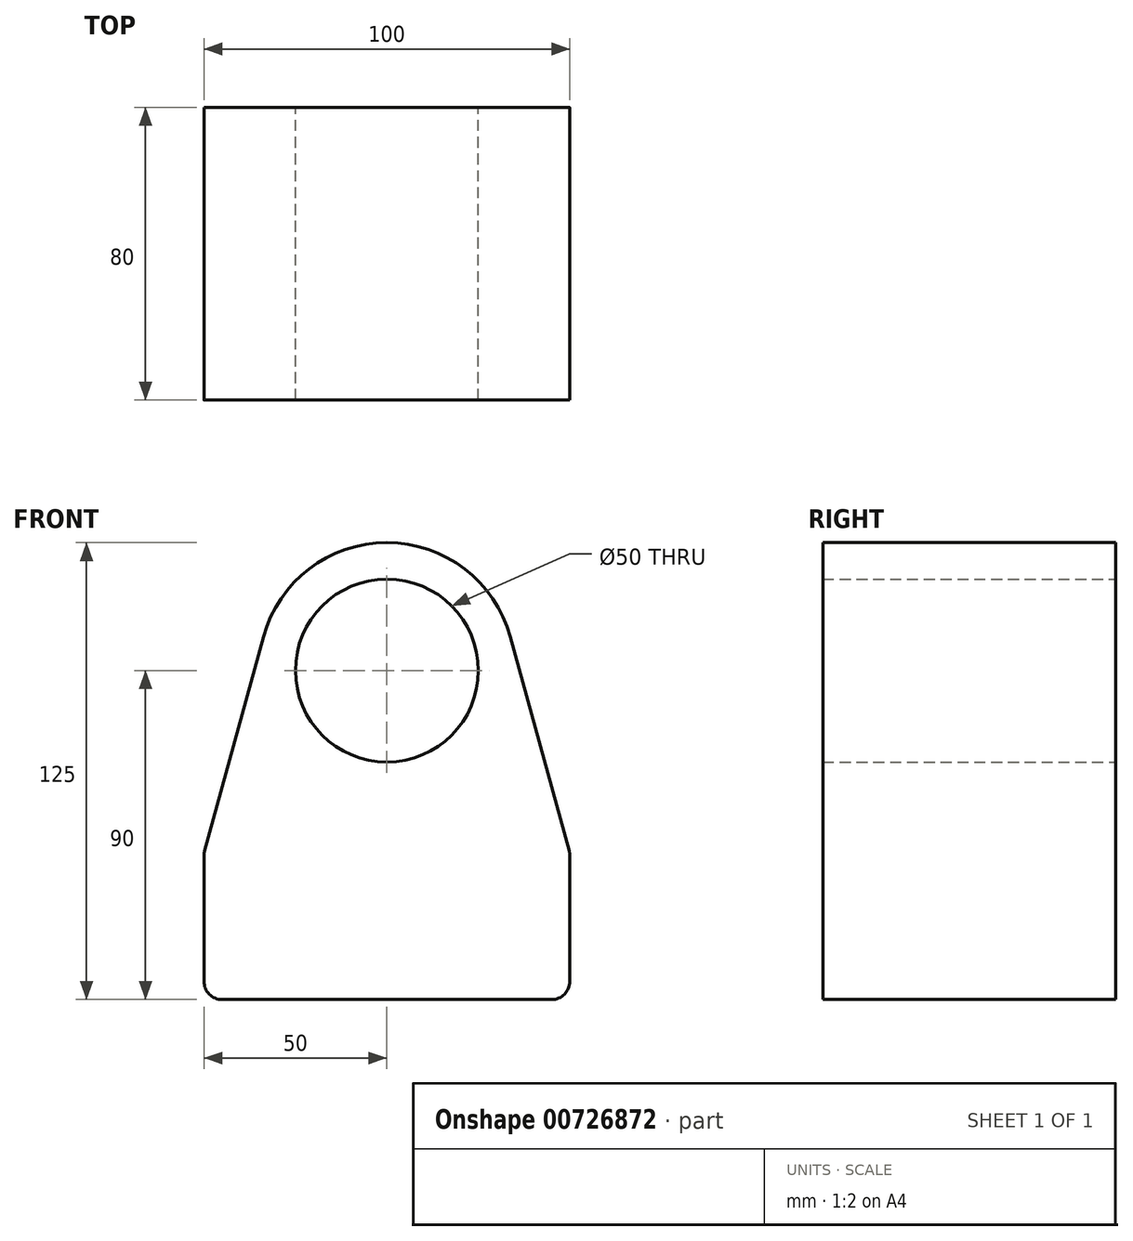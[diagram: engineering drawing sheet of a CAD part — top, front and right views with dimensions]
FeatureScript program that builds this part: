
annotation { "Feature Type Name" : "Feature", "Feature Type Description" : "" }
export const myFeature = defineFeature(function(context is Context, id is Id, definition is map)
    precondition{}
    {
        {
            var Q0;
            Q0=qCreatedBy(makeId("Front.planeOp"),FACE);
            var sketch = newSketch(context, id + "F0", { "sketchPlane" : qUnion([Q0])});
            skLineSegment(sketch, "E0", {"start": v(0, 0) * mm, "end": v(0, 40) * mm});
            skLineSegment(sketch, "E1", {"start": v(100, 40) * mm, "end": v(100, 0) * mm});
            skLineSegment(sketch, "E2", {"start": v(100, 0) * mm, "end": v(0, 0) * mm});
            skCircle(sketch, "E3", {"center": v(50, 90) * mm, "radius": 25 * mm});
            skArc(sketch, "E4", {"start": v(83.75, 99.25) * mm, "mid": v(50, 125) * mm, "end": v(16.25, 99.25) * mm});
            skLineSegment(sketch, "E5", {"start": v(0, 40) * mm, "end": v(16.25, 99.25) * mm});
            skLineSegment(sketch, "E6", {"start": v(100, 40) * mm, "end": v(83.75, 99.25) * mm});
            skPoint(sketch, "E7.orphan", {"position": v(50, 40) * mm});
            skSolve(sketch);
        }
        {
            var Q0;
            Q0 = qSketchRegion(id + "F0", true);
            extrude(context, id + "F1", {"entities" : qUnion([Q0]), "depth" : 80 * mm, "offsetDistance" : 25 * mm});
        }
        {
            var Q0;
            Q0=makeQuery(id+"F1.opExtrude","SWEPT_EDGE",EDGE,{"disambiguationData":[OSD([sQuery(id+"F0.wireOp",EDGE,"E0"),sQuery(id+"F0.wireOp",EDGE,"E5")])]});
            var Q1;
            Q1=makeQuery(id+"F1.opExtrude","SWEPT_EDGE",EDGE,{"disambiguationData":[OSD([sQuery(id+"F0.wireOp",EDGE,"E1"),sQuery(id+"F0.wireOp",EDGE,"E6")])]});
            var Q2;
            Q2=makeQuery(id+"F1.opExtrude","SWEPT_EDGE",EDGE,{"disambiguationData":[OSD([sQuery(id+"F0.wireOp",EDGE,"E1"),sQuery(id+"F0.wireOp",EDGE,"E2")])]});
            var Q3;
            Q3=makeQuery(id+"F1.opExtrude","SWEPT_EDGE",EDGE,{"disambiguationData":[OSD([sQuery(id+"F0.wireOp",EDGE,"E0"),sQuery(id+"F0.wireOp",EDGE,"E2")])]});
            fillet(context, id + "F2", {"entities" : qUnion([Q0, Q1, Q2, Q3]), "radius" : 5 * mm, "tangentPropagation" : true, "allowEdgeOverflow" : false});
        }
    });
